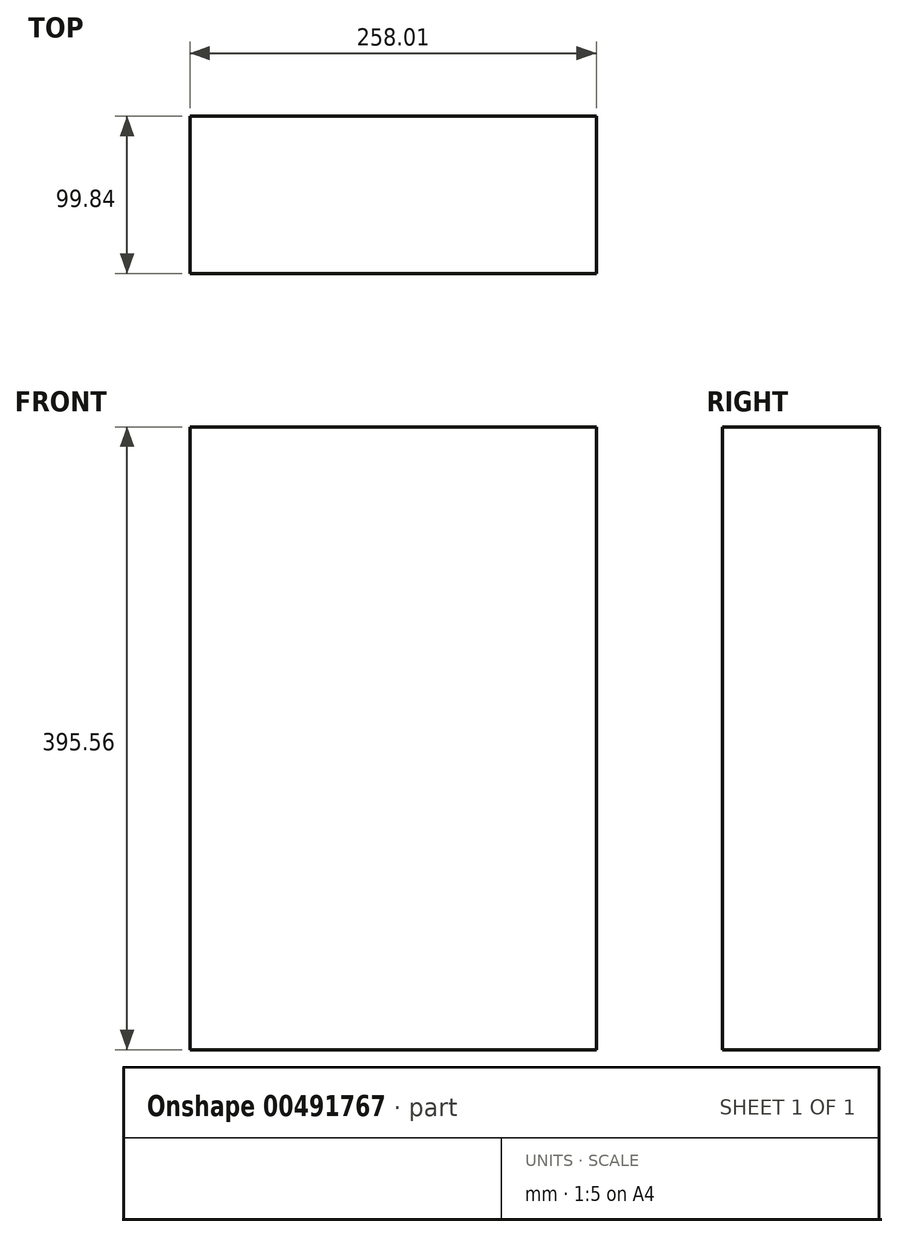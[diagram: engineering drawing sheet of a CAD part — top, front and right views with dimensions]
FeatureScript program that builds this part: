
annotation { "Feature Type Name" : "Feature", "Feature Type Description" : "" }
export const myFeature = defineFeature(function(context is Context, id is Id, definition is map)
    precondition{}
    {
        {
            var Q0;
            Q0=qCreatedBy(makeId("Front.planeOp"),FACE);
            var sketch = newSketch(context, id + "F0", { "sketchPlane" : qUnion([Q0])});
            skLineSegment(sketch, "E0.bottom", {"start": v(-194.2, 197.78) * mm, "end": v(63.81, 197.78) * mm});
            skLineSegment(sketch, "E0.top", {"start": v(-194.2, -197.78) * mm, "end": v(63.81, -197.78) * mm});
            skLineSegment(sketch, "E0.left", {"start": v(-194.2, 197.78) * mm, "end": v(-194.2, -197.78) * mm});
            skLineSegment(sketch, "E0.right", {"start": v(63.81, 197.78) * mm, "end": v(63.81, -197.78) * mm});
            skPoint(sketch, "E0.middle", {"position": v(-65.2, 0) * mm});
            skSolve(sketch);
        }
        {
            var Q0;
            Q0 = qSketchRegion(id + "F0", true);
            var sketch = newSketch(context, id + "F1", { "sketchPlane" : qUnion([Q0])});
            skSolve(sketch);
        }
        {
            var Q0;
            Q0=makeQuery(id+"F1.imprint","IMPRINT",FACE,{"disambiguationData":[TD([[makeQuery(id+"F1.imprint","IMPRINT",EDGE,{"derivedFrom":makeQuery(id+"F0.imprint","IMPRINT",EDGE,{"derivedFrom":sQuery(id+"F0.wireOp",EDGE,"E0.bottom")})}),-1.0]])]});
            extrude(context, id + "F2", {"entities" : qUnion([Q0]), "depth" : 99.84 * mm});
        }
    });
